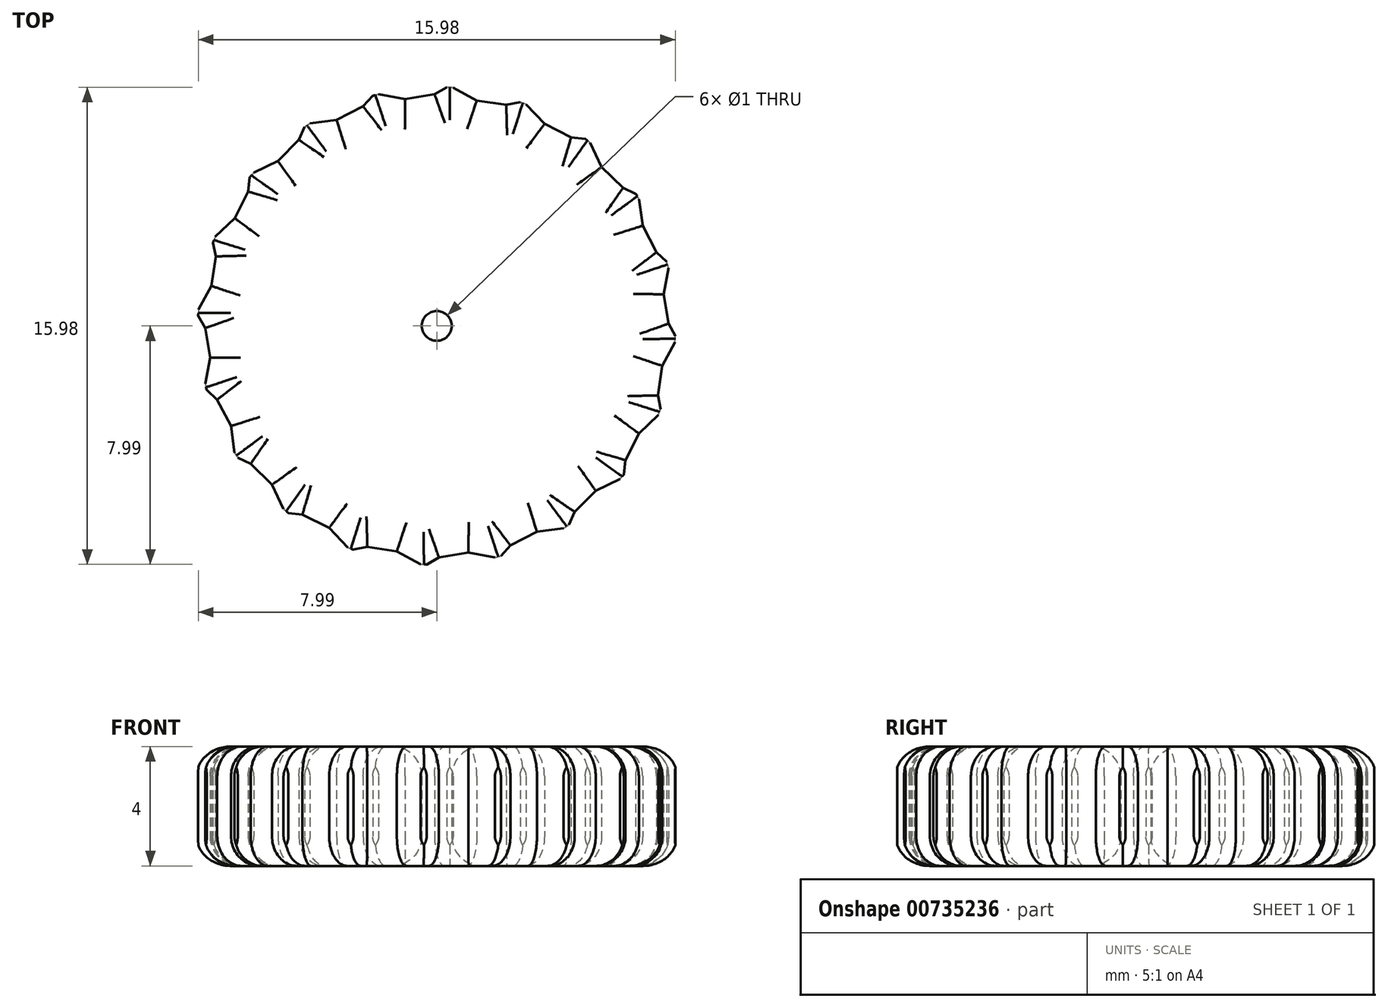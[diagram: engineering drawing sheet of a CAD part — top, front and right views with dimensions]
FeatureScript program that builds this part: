
annotation { "Feature Type Name" : "Feature", "Feature Type Description" : "" }
export const myFeature = defineFeature(function(context is Context, id is Id, definition is map)
    precondition{}
    {
        {
            var Q0;
            Q0=qCreatedBy(makeId("Top.planeOp"),FACE);
            var sketch = newSketch(context, id + "F0", { "sketchPlane" : qUnion([Q0])});
            skArc(sketch, "E0", {"start": v(-6.78, -4.25) * mm, "mid": v(-6.72, -4.34) * mm, "end": v(-6.67, -4.42) * mm});
            skCircle(sketch, "E1", {"center": v(0, 0) * mm, "radius": 0.5 * mm});
            skLineSegment(sketch, "E2", {"start": v(-6.78, -4.25) * mm, "end": v(-6.9, -3.35) * mm});
            skLineSegment(sketch, "E3", {"start": v(-6.9, -3.35) * mm, "end": v(-7.36, -2.47) * mm});
            skLineSegment(sketch, "E4", {"start": v(-7.36, -2.47) * mm, "end": v(-7.7, -2.15) * mm});
            skPoint(sketch, "E5.center", {"position": v(-0.1, -0.09) * mm});
            skLineSegment(sketch, "E6.1.0", {"start": v(-6.23, -4.62) * mm, "end": v(-6.67, -4.42) * mm});
            skLineSegment(sketch, "E6.1.1", {"start": v(-5.52, -5.32) * mm, "end": v(-6.23, -4.62) * mm});
            skLineSegment(sketch, "E6.1.2", {"start": v(-5.13, -6.14) * mm, "end": v(-5.52, -5.32) * mm});
            skLineSegment(sketch, "E6.2.0", {"start": v(-4.5, -6.32) * mm, "end": v(-4.97, -6.27) * mm});
            skLineSegment(sketch, "E6.2.1", {"start": v(-3.6, -6.77) * mm, "end": v(-4.5, -6.32) * mm});
            skLineSegment(sketch, "E6.2.2", {"start": v(-2.99, -7.42) * mm, "end": v(-3.6, -6.77) * mm});
            skLineSegment(sketch, "E6.3.0", {"start": v(-2.33, -7.4) * mm, "end": v(-2.8, -7.5) * mm});
            skLineSegment(sketch, "E6.3.1", {"start": v(-1.34, -7.55) * mm, "end": v(-2.33, -7.4) * mm});
            skLineSegment(sketch, "E6.3.2", {"start": v(-0.55, -7.98) * mm, "end": v(-1.34, -7.55) * mm});
            skLineSegment(sketch, "E6.4.0", {"start": v(0.07, -7.76) * mm, "end": v(-0.34, -8) * mm});
            skLineSegment(sketch, "E6.4.1", {"start": v(1.06, -7.6) * mm, "end": v(0.07, -7.76) * mm});
            skLineSegment(sketch, "E6.4.2", {"start": v(1.95, -7.76) * mm, "end": v(1.06, -7.6) * mm});
            skLineSegment(sketch, "E6.5.0", {"start": v(2.47, -7.36) * mm, "end": v(2.15, -7.7) * mm});
            skLineSegment(sketch, "E6.5.1", {"start": v(3.35, -6.9) * mm, "end": v(2.47, -7.36) * mm});
            skLineSegment(sketch, "E6.5.2", {"start": v(4.25, -6.78) * mm, "end": v(3.35, -6.9) * mm});
            skLineSegment(sketch, "E6.6.0", {"start": v(4.62, -6.23) * mm, "end": v(4.42, -6.67) * mm});
            skLineSegment(sketch, "E6.6.1", {"start": v(5.32, -5.52) * mm, "end": v(4.62, -6.23) * mm});
            skLineSegment(sketch, "E6.6.2", {"start": v(6.14, -5.13) * mm, "end": v(5.32, -5.52) * mm});
            skLineSegment(sketch, "E6.7.0", {"start": v(6.32, -4.5) * mm, "end": v(6.27, -4.97) * mm});
            skLineSegment(sketch, "E6.7.1", {"start": v(6.77, -3.6) * mm, "end": v(6.32, -4.5) * mm});
            skLineSegment(sketch, "E6.7.2", {"start": v(7.42, -2.99) * mm, "end": v(6.77, -3.6) * mm});
            skLineSegment(sketch, "E6.8.0", {"start": v(7.4, -2.33) * mm, "end": v(7.5, -2.8) * mm});
            skLineSegment(sketch, "E6.8.1", {"start": v(7.55, -1.34) * mm, "end": v(7.4, -2.33) * mm});
            skLineSegment(sketch, "E6.8.2", {"start": v(7.98, -0.55) * mm, "end": v(7.55, -1.34) * mm});
            skLineSegment(sketch, "E6.9.0", {"start": v(7.76, 0.07) * mm, "end": v(8, -0.34) * mm});
            skLineSegment(sketch, "E6.9.1", {"start": v(7.6, 1.06) * mm, "end": v(7.76, 0.07) * mm});
            skLineSegment(sketch, "E6.9.2", {"start": v(7.76, 1.95) * mm, "end": v(7.6, 1.06) * mm});
            skLineSegment(sketch, "E6.10.0", {"start": v(7.36, 2.47) * mm, "end": v(7.7, 2.15) * mm});
            skLineSegment(sketch, "E6.10.1", {"start": v(6.9, 3.35) * mm, "end": v(7.36, 2.47) * mm});
            skLineSegment(sketch, "E6.10.2", {"start": v(6.78, 4.25) * mm, "end": v(6.9, 3.35) * mm});
            skLineSegment(sketch, "E6.11.0", {"start": v(6.23, 4.62) * mm, "end": v(6.67, 4.42) * mm});
            skLineSegment(sketch, "E6.11.1", {"start": v(5.52, 5.32) * mm, "end": v(6.23, 4.62) * mm});
            skLineSegment(sketch, "E6.11.2", {"start": v(5.13, 6.14) * mm, "end": v(5.52, 5.32) * mm});
            skLineSegment(sketch, "E6.12.0", {"start": v(4.5, 6.32) * mm, "end": v(4.97, 6.27) * mm});
            skLineSegment(sketch, "E6.12.1", {"start": v(3.6, 6.77) * mm, "end": v(4.5, 6.32) * mm});
            skLineSegment(sketch, "E6.12.2", {"start": v(2.99, 7.42) * mm, "end": v(3.6, 6.77) * mm});
            skLineSegment(sketch, "E6.13.0", {"start": v(2.33, 7.4) * mm, "end": v(2.8, 7.5) * mm});
            skLineSegment(sketch, "E6.13.1", {"start": v(1.34, 7.55) * mm, "end": v(2.33, 7.4) * mm});
            skLineSegment(sketch, "E6.13.2", {"start": v(0.55, 7.98) * mm, "end": v(1.34, 7.55) * mm});
            skLineSegment(sketch, "E6.14.0", {"start": v(-0.07, 7.76) * mm, "end": v(0.34, 8) * mm});
            skLineSegment(sketch, "E6.14.1", {"start": v(-1.06, 7.6) * mm, "end": v(-0.07, 7.76) * mm});
            skLineSegment(sketch, "E6.14.2", {"start": v(-1.95, 7.76) * mm, "end": v(-1.06, 7.6) * mm});
            skLineSegment(sketch, "E6.15.0", {"start": v(-2.47, 7.36) * mm, "end": v(-2.15, 7.7) * mm});
            skLineSegment(sketch, "E6.15.1", {"start": v(-3.35, 6.9) * mm, "end": v(-2.47, 7.36) * mm});
            skLineSegment(sketch, "E6.15.2", {"start": v(-4.25, 6.78) * mm, "end": v(-3.35, 6.9) * mm});
            skLineSegment(sketch, "E6.16.0", {"start": v(-4.62, 6.23) * mm, "end": v(-4.42, 6.67) * mm});
            skLineSegment(sketch, "E6.16.1", {"start": v(-5.32, 5.52) * mm, "end": v(-4.62, 6.23) * mm});
            skLineSegment(sketch, "E6.16.2", {"start": v(-6.14, 5.13) * mm, "end": v(-5.32, 5.52) * mm});
            skLineSegment(sketch, "E6.17.0", {"start": v(-6.32, 4.5) * mm, "end": v(-6.27, 4.97) * mm});
            skLineSegment(sketch, "E6.17.1", {"start": v(-6.77, 3.6) * mm, "end": v(-6.32, 4.5) * mm});
            skLineSegment(sketch, "E6.17.2", {"start": v(-7.42, 2.99) * mm, "end": v(-6.77, 3.6) * mm});
            skLineSegment(sketch, "E6.18.0", {"start": v(-7.4, 2.33) * mm, "end": v(-7.5, 2.8) * mm});
            skLineSegment(sketch, "E6.18.1", {"start": v(-7.55, 1.34) * mm, "end": v(-7.4, 2.33) * mm});
            skLineSegment(sketch, "E6.18.2", {"start": v(-7.98, 0.55) * mm, "end": v(-7.55, 1.34) * mm});
            skLineSegment(sketch, "E6.19.0", {"start": v(-7.76, -0.07) * mm, "end": v(-8, 0.34) * mm});
            skLineSegment(sketch, "E6.19.1", {"start": v(-7.6, -1.06) * mm, "end": v(-7.76, -0.07) * mm});
            skLineSegment(sketch, "E6.19.2", {"start": v(-7.76, -1.95) * mm, "end": v(-7.6, -1.06) * mm});
            skArc(sketch, "E7.trimOffspring", {"start": v(-7.42, 2.99) * mm, "mid": v(-7.46, 2.89) * mm, "end": v(-7.5, 2.8) * mm});
            skArc(sketch, "E8.trimOffspring", {"start": v(-7.98, 0.55) * mm, "mid": v(-7.99, 0.44) * mm, "end": v(-8, 0.34) * mm});
            skArc(sketch, "E9.trimOffspring", {"start": v(-7.76, -1.95) * mm, "mid": v(-7.73, -2.05) * mm, "end": v(-7.7, -2.15) * mm});
            skArc(sketch, "E10.trimOffspring", {"start": v(-6.14, 5.13) * mm, "mid": v(-6.2, 5.05) * mm, "end": v(-6.27, 4.97) * mm});
            skArc(sketch, "E11.trimOffspring", {"start": v(-4.25, 6.78) * mm, "mid": v(-4.34, 6.72) * mm, "end": v(-4.42, 6.67) * mm});
            skArc(sketch, "E12.trimOffspring", {"start": v(-1.95, 7.76) * mm, "mid": v(-2.05, 7.73) * mm, "end": v(-2.15, 7.7) * mm});
            skArc(sketch, "E13.trimOffspring", {"start": v(0.55, 7.98) * mm, "mid": v(0.44, 7.99) * mm, "end": v(0.34, 8) * mm});
            skArc(sketch, "E14.trimOffspring", {"start": v(2.99, 7.42) * mm, "mid": v(2.89, 7.46) * mm, "end": v(2.8, 7.5) * mm});
            skArc(sketch, "E15.trimOffspring", {"start": v(5.13, 6.14) * mm, "mid": v(5.05, 6.2) * mm, "end": v(4.97, 6.27) * mm});
            skArc(sketch, "E16.trimOffspring", {"start": v(6.78, 4.25) * mm, "mid": v(6.72, 4.34) * mm, "end": v(6.67, 4.42) * mm});
            skArc(sketch, "E17.trimOffspring", {"start": v(7.76, 1.95) * mm, "mid": v(7.73, 2.05) * mm, "end": v(7.7, 2.15) * mm});
            skArc(sketch, "E18.trimOffspring", {"start": v(7.98, -0.55) * mm, "mid": v(7.99, -0.44) * mm, "end": v(8, -0.34) * mm});
            skArc(sketch, "E19.trimOffspring", {"start": v(7.42, -2.99) * mm, "mid": v(7.46, -2.89) * mm, "end": v(7.5, -2.8) * mm});
            skArc(sketch, "E20.trimOffspring", {"start": v(6.14, -5.13) * mm, "mid": v(6.2, -5.05) * mm, "end": v(6.27, -4.97) * mm});
            skArc(sketch, "E21.trimOffspring", {"start": v(4.25, -6.78) * mm, "mid": v(4.34, -6.72) * mm, "end": v(4.42, -6.67) * mm});
            skArc(sketch, "E22.trimOffspring", {"start": v(1.95, -7.76) * mm, "mid": v(2.05, -7.73) * mm, "end": v(2.15, -7.7) * mm});
            skArc(sketch, "E23.trimOffspring", {"start": v(-0.55, -7.98) * mm, "mid": v(-0.44, -7.99) * mm, "end": v(-0.34, -8) * mm});
            skArc(sketch, "E24.trimOffspring", {"start": v(-2.99, -7.42) * mm, "mid": v(-2.89, -7.46) * mm, "end": v(-2.8, -7.5) * mm});
            skArc(sketch, "E25.trimOffspring", {"start": v(-5.13, -6.14) * mm, "mid": v(-5.05, -6.2) * mm, "end": v(-4.97, -6.27) * mm});
            skSolve(sketch);
        }
        {
            var Q0;
            Q0 = qSketchRegion(id + "F0", true);
            extrude(context, id + "F1", {"entities" : qUnion([Q0]), "depth" : 4 * mm, "offsetDistance" : 25 * mm});
        }
        {
            var Q0;
            Q0=makeQuery(id+"F1.opExtrude","CAP_FACE",FACE,{"disambiguationData":[OSD([sQuery(id+"F0.wireOp",EDGE,"E0"),sQuery(id+"F0.wireOp",EDGE,"E1")])],"isStart":false});
            fillet(context, id + "F2", {"entities" : qUnion([Q0]), "radius" : 1 * mm, "tangentPropagation" : true, "allowEdgeOverflow" : false});
        }
        {
            var Q0;
            Q0=makeQuery(id+"F1.opExtrude","CAP_FACE",FACE,{"disambiguationData":[OSD([sQuery(id+"F0.wireOp",EDGE,"E0"),sQuery(id+"F0.wireOp",EDGE,"E1")])],"isStart":true});
            fillet(context, id + "F3", {"entities" : qUnion([Q0]), "radius" : 1 * mm, "tangentPropagation" : true, "allowEdgeOverflow" : false});
        }
    });
